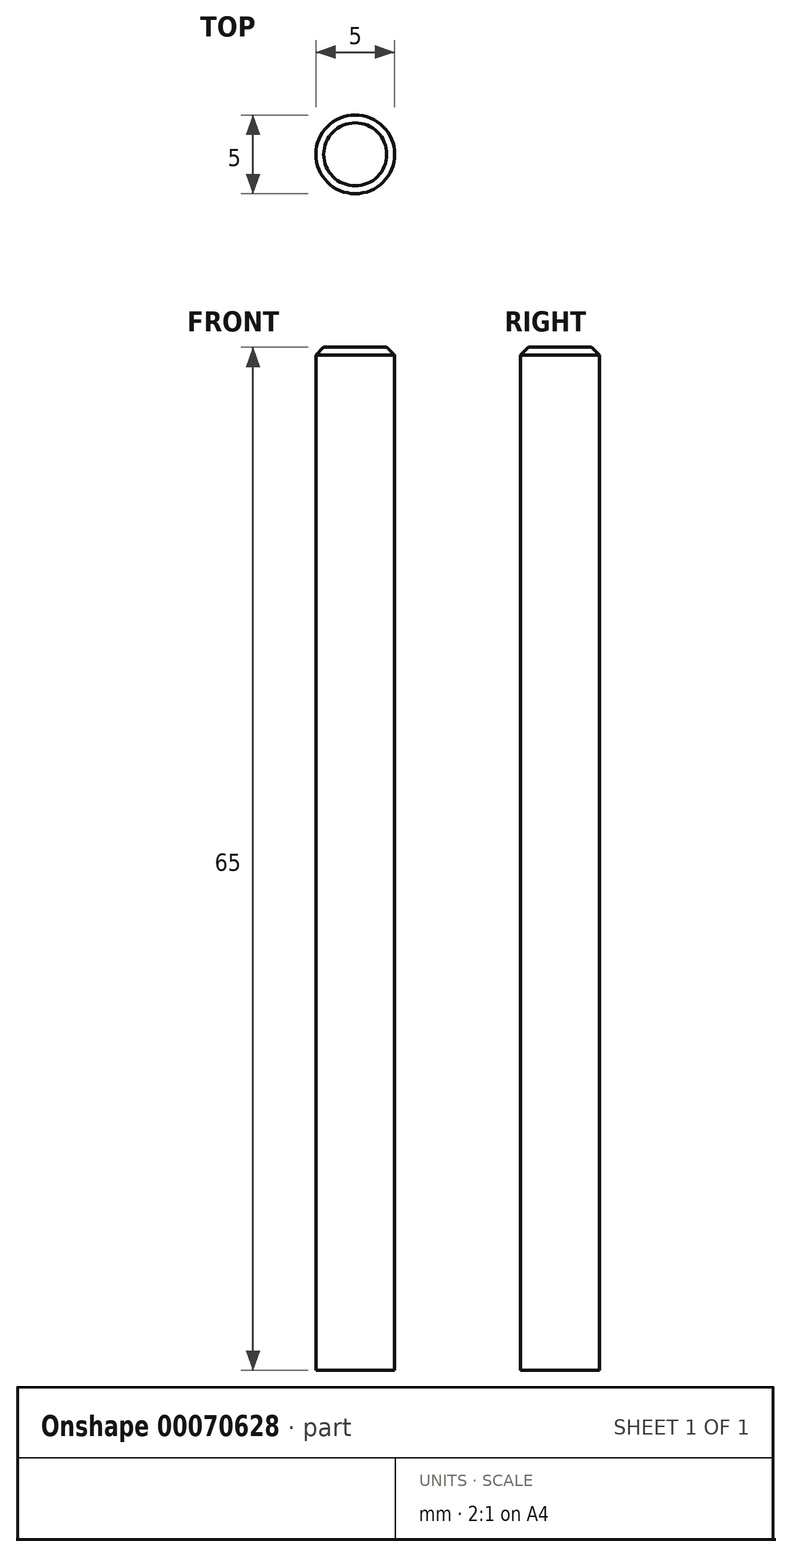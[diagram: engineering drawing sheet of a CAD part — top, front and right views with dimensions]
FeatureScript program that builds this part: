
annotation { "Feature Type Name" : "Feature", "Feature Type Description" : "" }
export const myFeature = defineFeature(function(context is Context, id is Id, definition is map)
    precondition{}
    {
        {
            var Q0;
            Q0=qCreatedBy(makeId("Top.planeOp"),FACE);
            var sketch = newSketch(context, id + "F0", { "sketchPlane" : qUnion([Q0])});
            skCircle(sketch, "E0", {"center": v(0, 0) * mm, "radius": 2.5 * mm});
            skSolve(sketch);
        }
        {
            var Q0;
            Q0=qSketchRegion(id+"F0",true);
            extrude(context, id + "F1", {"entities" : qUnion([Q0]), "depth" : 65 * mm});
        }
        {
            var Q0;
            Q0=makeQuery(id+"F1.opExtrude","CAP_EDGE",EDGE,{"disambiguationData":[OSD([sQuery(id+"F0.wireOp",EDGE,"E0")])],"isStart":false});
            chamfer(context, id + "F2", {"entities" : qUnion([Q0]), "width" : 0.5 * mm, "tangentPropagation" : true});
        }
    });
